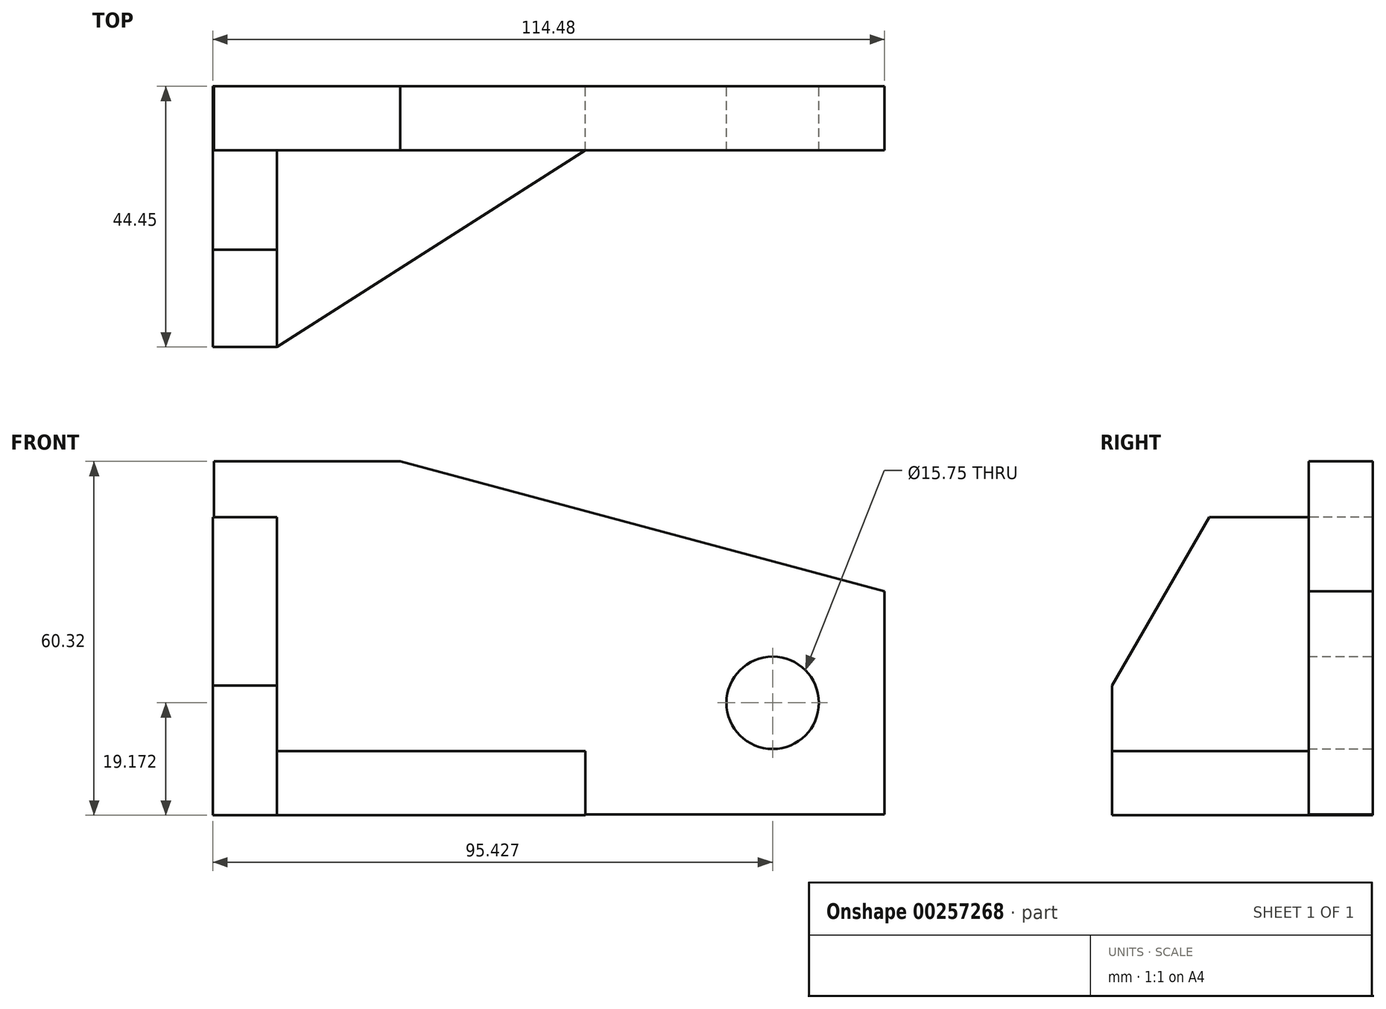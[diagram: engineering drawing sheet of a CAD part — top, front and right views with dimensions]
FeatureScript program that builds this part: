
annotation { "Feature Type Name" : "Feature", "Feature Type Description" : "" }
export const myFeature = defineFeature(function(context is Context, id is Id, definition is map)
    precondition{}
    {
        {
            var Q0;
            Q0=qCreatedBy(makeId("Front.planeOp"),FACE);
            var sketch = newSketch(context, id + "F0", { "sketchPlane" : qUnion([Q0])});
            skLineSegment(sketch, "E0", {"start": v(22.09, 0) * mm, "end": v(22.09, -60.2) * mm});
            skLineSegment(sketch, "E1", {"start": v(22.09, -60.2) * mm, "end": v(-92.21, -60.2) * mm});
            skLineSegment(sketch, "E2", {"start": v(-92.21, -60.2) * mm, "end": v(-92.21, 0) * mm});
            skLineSegment(sketch, "E3", {"start": v(-92.21, 0) * mm, "end": v(-60.46, 0) * mm});
            skLineSegment(sketch, "E4", {"start": v(-60.46, 0) * mm, "end": v(22.09, -22.12) * mm});
            skLineSegment(sketch, "E5", {"start": v(22.09, 0) * mm, "end": v(22.09, -22.12) * mm});
            skLineSegment(sketch, "E6", {"start": v(22.09, 0) * mm, "end": v(-60.46, 0) * mm, "construction": true});
            skLineSegment(sketch, "E7", {"start": v(22.09, -60.2) * mm, "end": v(3.04, -60.2) * mm});
            skLineSegment(sketch, "E8", {"start": v(3.04, -60.2) * mm, "end": v(3.04, -41.15) * mm, "construction": true});
            skCircle(sketch, "E9", {"center": v(3.04, -41.15) * mm, "radius": 7.87 * mm});
            skSolve(sketch);
        }
        {
            var Q0;
            Q0 = qSketchRegion(id + "F0", true);
            extrude(context, id + "F1", {"entities" : qUnion([Q0]), "depth" : 10.92 * mm});
        }
        {
            var Q0;
            Q0=qCreatedBy(makeId("Front.planeOp"),FACE);
            var sketch = newSketch(context, id + "F2", { "sketchPlane" : qUnion([Q0])});
            skLineSegment(sketch, "E10", {"start": v(-92.4, -60.32) * mm, "end": v(-81.47, -60.32) * mm});
            skLineSegment(sketch, "E11", {"start": v(-81.47, -60.32) * mm, "end": v(-28.9, -60.32) * mm});
            skLineSegment(sketch, "E12", {"start": v(-92.4, -60.32) * mm, "end": v(-92.4, -9.52) * mm});
            skLineSegment(sketch, "E13", {"start": v(-81.47, -9.52) * mm, "end": v(-92.4, -9.52) * mm});
            skLineSegment(sketch, "E14", {"start": v(-81.47, -9.52) * mm, "end": v(-81.47, -60.32) * mm});
            skLineSegment(sketch, "E15", {"start": v(-28.9, -60.32) * mm, "end": v(-28.9, -49.4) * mm});
            skLineSegment(sketch, "E16", {"start": v(-28.9, -49.4) * mm, "end": v(-81.47, -49.4) * mm});
            skLineSegment(sketch, "E17", {"start": v(-81.47, -60.32) * mm, "end": v(-81.47, -38.22) * mm});
            skLineSegment(sketch, "E18", {"start": v(-92.4, -38.22) * mm, "end": v(-81.47, -38.22) * mm});
            skSolve(sketch);
        }
        {
            var Q0;
            Q0 = qSketchRegion(id + "F2", true);
            extrude(context, id + "F3", {"entities" : qUnion([Q0]), "operationType" : NewBodyOperationType.ADD, "depth" : 44.45 * mm});
        }
        {
            var Q0;
            Q0=makeQuery(id+"F3.opExtrude","SWEPT_FACE",FACE,{"disambiguationData":[OSD([sQuery(id+"F2.wireOp",EDGE,"E16")])]});
            var sketch = newSketch(context, id + "F4", { "sketchPlane" : qUnion([Q0])});
            skLineSegment(sketch, "E19", {"start": v(-28.9, -10.92) * mm, "end": v(-81.47, -44.45) * mm});
            skSolve(sketch);
        }
        {
            var Q0;
            Q0=makeQuery(id+"F4.imprint","IMPRINT",FACE,{"disambiguationData":[TD([[makeQuery(id+"F4.imprint","IMPRINT",EDGE,{"derivedFrom":sQuery(id+"F4.wireOp",EDGE,"E19")}),1.0]])]});
            extrude(context, id + "F5", {"entities" : qUnion([Q0]), "operationType" : NewBodyOperationType.REMOVE, "oppositeDirection" : true, "depth" : 10.92 * mm});
        }
        {
            var Q0;
            Q0=makeQuery(id+"F3.opExtrude","CAP_EDGE",EDGE,{"disambiguationData":[OSD([sQuery(id+"F2.wireOp",EDGE,"E13")])],"isStart":false});
            chamfer(context, id + "F6", {"entities" : qUnion([Q0]), "chamferType" : ChamferType.OFFSET_ANGLE, "width" : 28.7 * mm, "oppositeDirection" : false, "angle" : 30 * degree, "tangentPropagation" : true});
        }
    });
